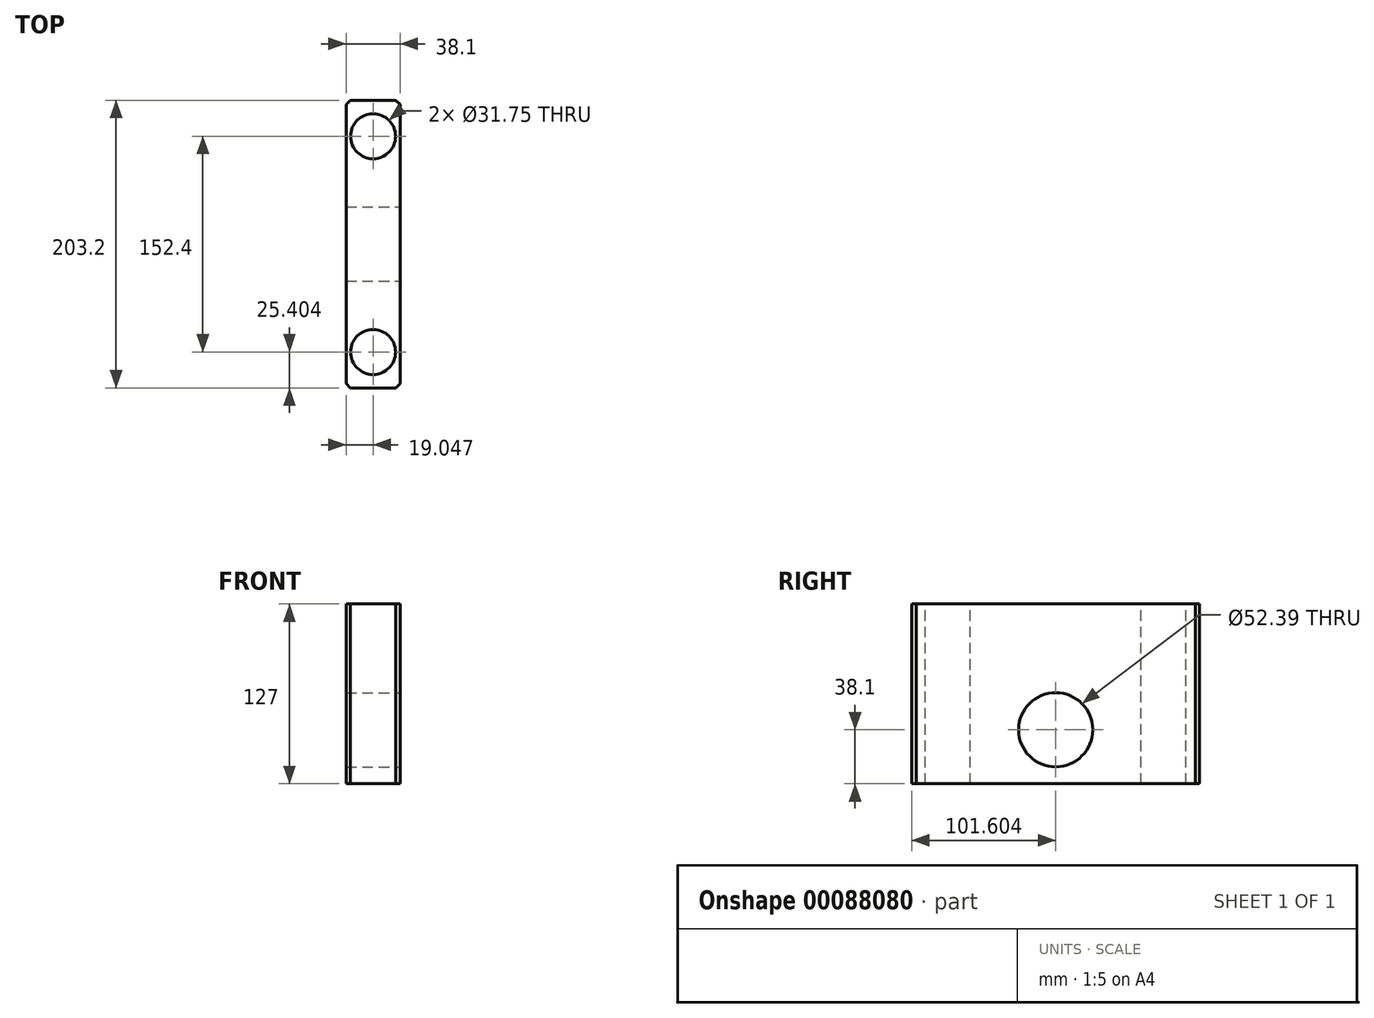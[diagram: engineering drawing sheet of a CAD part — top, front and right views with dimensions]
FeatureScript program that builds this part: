
annotation { "Feature Type Name" : "Feature", "Feature Type Description" : "" }
export const myFeature = defineFeature(function(context is Context, id is Id, definition is map)
    precondition{}
    {
        {
            var Q0;
            Q0=qCreatedBy(makeId("Top.planeOp"),FACE);
            var sketch = newSketch(context, id + "F0", { "sketchPlane" : qUnion([Q0])});
            skLineSegment(sketch, "E0.bottom", {"start": v(-181.82, 18.66) * mm, "end": v(21.38, 18.66) * mm});
            skLineSegment(sketch, "E0.top", {"start": v(-181.82, -19.44) * mm, "end": v(21.38, -19.44) * mm});
            skLineSegment(sketch, "E0.left", {"start": v(-181.82, 18.66) * mm, "end": v(-181.82, -19.44) * mm});
            skLineSegment(sketch, "E0.right", {"start": v(21.38, 18.66) * mm, "end": v(21.38, -19.44) * mm});
            skSolve(sketch);
        }
        {
            var Q0;
            Q0=makeQuery(id+"F0.imprint","IMPRINT",FACE,{"disambiguationData":[TD([[makeQuery(id+"F0.imprint","IMPRINT",EDGE,{"derivedFrom":sQuery(id+"F0.wireOp",EDGE,"E0.bottom")}),-1.0]])]});
            extrude(context, id + "F1", {"entities" : qUnion([Q0]), "depth" : 127 * mm});
        }
        {
            var Q0;
            Q0=makeQuery(id+"F1.opExtrude","CAP_FACE",FACE,{"disambiguationData":[OSD([sQuery(id+"F0.wireOp",EDGE,"E0.bottom"),sQuery(id+"F0.wireOp",EDGE,"E0.top"),sQuery(id+"F0.wireOp",EDGE,"E0.left"),sQuery(id+"F0.wireOp",EDGE,"E0.right")])],"isStart":false});
            var sketch = newSketch(context, id + "F2", { "sketchPlane" : qUnion([Q0])});
            skLineSegment(sketch, "E1", {"start": v(-181.82, -0.4) * mm, "end": v(-131.02, -0.4) * mm, "construction": true});
            skLineSegment(sketch, "E2", {"start": v(-80.22, -19.44) * mm, "end": v(-80.22, 18.66) * mm, "construction": true});
            skLineSegment(sketch, "E3", {"start": v(-131.02, -19.44) * mm, "end": v(-131.02, 18.66) * mm});
            skLineSegment(sketch, "E4", {"start": v(-29.42, -19.44) * mm, "end": v(-29.42, 18.66) * mm, "construction": true});
            skLineSegment(sketch, "E5.trimOffspring", {"start": v(-29.42, -0.4) * mm, "end": v(21.38, -0.4) * mm, "construction": true});
            skCircle(sketch, "E6", {"center": v(-4.02, -0.4) * mm, "radius": 15.88 * mm});
            skCircle(sketch, "E7", {"center": v(-156.42, -0.4) * mm, "radius": 15.88 * mm});
            skSolve(sketch);
        }
        {
            var Q0;
            Q0=makeQuery(id+"F2.imprint","IMPRINT",FACE,{"disambiguationData":[TD([[makeQuery(id+"F2.imprint","IMPRINT",EDGE,{"derivedFrom":sQuery(id+"F2.wireOp",EDGE,"E7")}),1.0]])]});
            var Q1;
            Q1=makeQuery(id+"F2.imprint","IMPRINT",FACE,{"disambiguationData":[TD([[makeQuery(id+"F2.imprint","IMPRINT",EDGE,{"derivedFrom":sQuery(id+"F2.wireOp",EDGE,"E6")}),1.0]])]});
            extrude(context, id + "F3", {"entities" : qUnion([Q0, Q1]), "operationType" : NewBodyOperationType.REMOVE, "endBound" : BoundingType.THROUGH_ALL, "oppositeDirection" : true, "depth" : 25.4 * mm});
        }
        {
            var Q0;
            Q0=makeQuery(id+"F1.opExtrude","SWEPT_EDGE",EDGE,{"disambiguationData":[OSD([sQuery(id+"F0.wireOp",EDGE,"E0.top"),sQuery(id+"F0.wireOp",EDGE,"E0.left")])]});
            var Q1;
            Q1=makeQuery(id+"F1.opExtrude","SWEPT_EDGE",EDGE,{"disambiguationData":[OSD([sQuery(id+"F0.wireOp",EDGE,"E0.top"),sQuery(id+"F0.wireOp",EDGE,"E0.right")])]});
            var Q2;
            Q2=makeQuery(id+"F1.opExtrude","SWEPT_EDGE",EDGE,{"disambiguationData":[OSD([sQuery(id+"F0.wireOp",EDGE,"E0.bottom"),sQuery(id+"F0.wireOp",EDGE,"E0.right")])]});
            var Q3;
            Q3=makeQuery(id+"F1.opExtrude","SWEPT_EDGE",EDGE,{"disambiguationData":[OSD([sQuery(id+"F0.wireOp",EDGE,"E0.bottom"),sQuery(id+"F0.wireOp",EDGE,"E0.left")])]});
            chamfer(context, id + "F4", {"entities" : qUnion([Q0, Q1, Q2, Q3]), "width" : 3.05 * mm, "tangentPropagation" : true});
        }
        {
            var Q0;
            Q0=makeQuery(id+"F1.opExtrude","SWEPT_FACE",FACE,{"disambiguationData":[OSD([sQuery(id+"F0.wireOp",EDGE,"E0.top")])]});
            var sketch = newSketch(context, id + "F5", { "sketchPlane" : qUnion([Q0])});
            skPoint(sketch, "E8.end.orphan", {"position": v(-80.22, 127) * mm});
            skPoint(sketch, "E9.orphan", {"position": v(-178.78, 63.5) * mm});
            skPoint(sketch, "E10.end.orphan", {"position": v(18.33, 63.5) * mm});
            skPoint(sketch, "E11.end.orphan", {"position": v(-80.22, 0) * mm});
            skLineSegment(sketch, "E12", {"start": v(-178.78, 76.2) * mm, "end": v(18.33, 76.2) * mm, "construction": true});
            skLineSegment(sketch, "E13", {"start": v(-80.22, 76.2) * mm, "end": v(-80.22, 0) * mm, "construction": true});
            skCircle(sketch, "E14", {"center": v(-80.22, 38.1) * mm, "radius": 26.2 * mm});
            skCircle(sketch, "E15", {"center": v(-80.22, 38.1) * mm, "radius": 19.05 * mm, "construction": true});
            skCircle(sketch, "E16", {"center": v(-80.22, 38.1) * mm, "radius": 15.88 * mm, "construction": true});
            skSolve(sketch);
        }
        {
            var Q0;
            Q0=makeQuery(id+"F5.imprint","IMPRINT",FACE,{"disambiguationData":[TD([[makeQuery(id+"F5.imprint","IMPRINT",EDGE,{"derivedFrom":sQuery(id+"F5.wireOp",EDGE,"E14")}),1.0]])]});
            extrude(context, id + "F6", {"entities" : qUnion([Q0]), "operationType" : NewBodyOperationType.REMOVE, "endBound" : BoundingType.THROUGH_ALL, "oppositeDirection" : true, "depth" : 25.4 * mm});
        }
        {
            var Q0;
            Q0=makeQuery(id+"F1.opExtrude","SWEPT_BODY",BODY,{"disambiguationData":[OSD([sQuery(id+"F0.wireOp",EDGE,"E0.bottom"),sQuery(id+"F0.wireOp",EDGE,"E0.top"),sQuery(id+"F0.wireOp",EDGE,"E0.left"),sQuery(id+"F0.wireOp",EDGE,"E0.right")])]});
            var Q1;
            {var subQ0=sQuery(id+"F0.wireOp",EDGE,"E0.top");Q1=makeQuery(id+"F4.opChamfer","BLEND_EDGE",EDGE,{"blendedFrom":[makeQuery(id+"F1.opExtrude","SWEPT_EDGE",EDGE,{"disambiguationData":[OSD([subQ0,sQuery(id+"F0.wireOp",EDGE,"E0.right")])]}),makeQuery(id+"F1.opExtrude","SWEPT_FACE",FACE,{"disambiguationData":[OSD([subQ0])]})],"blendedInto":[makeQuery(id+"F1.opExtrude","SWEPT_FACE",FACE,{"disambiguationData":[OSD([subQ0])]})]});}
            transform(context, id + "F7", {"entities" : qUnion([Q0]), "transformType" : TransformType.ROTATION, "transformAxis" : qUnion([Q1]), "angle" : 90 * degree, "makeCopy" : false});
        }
    });
